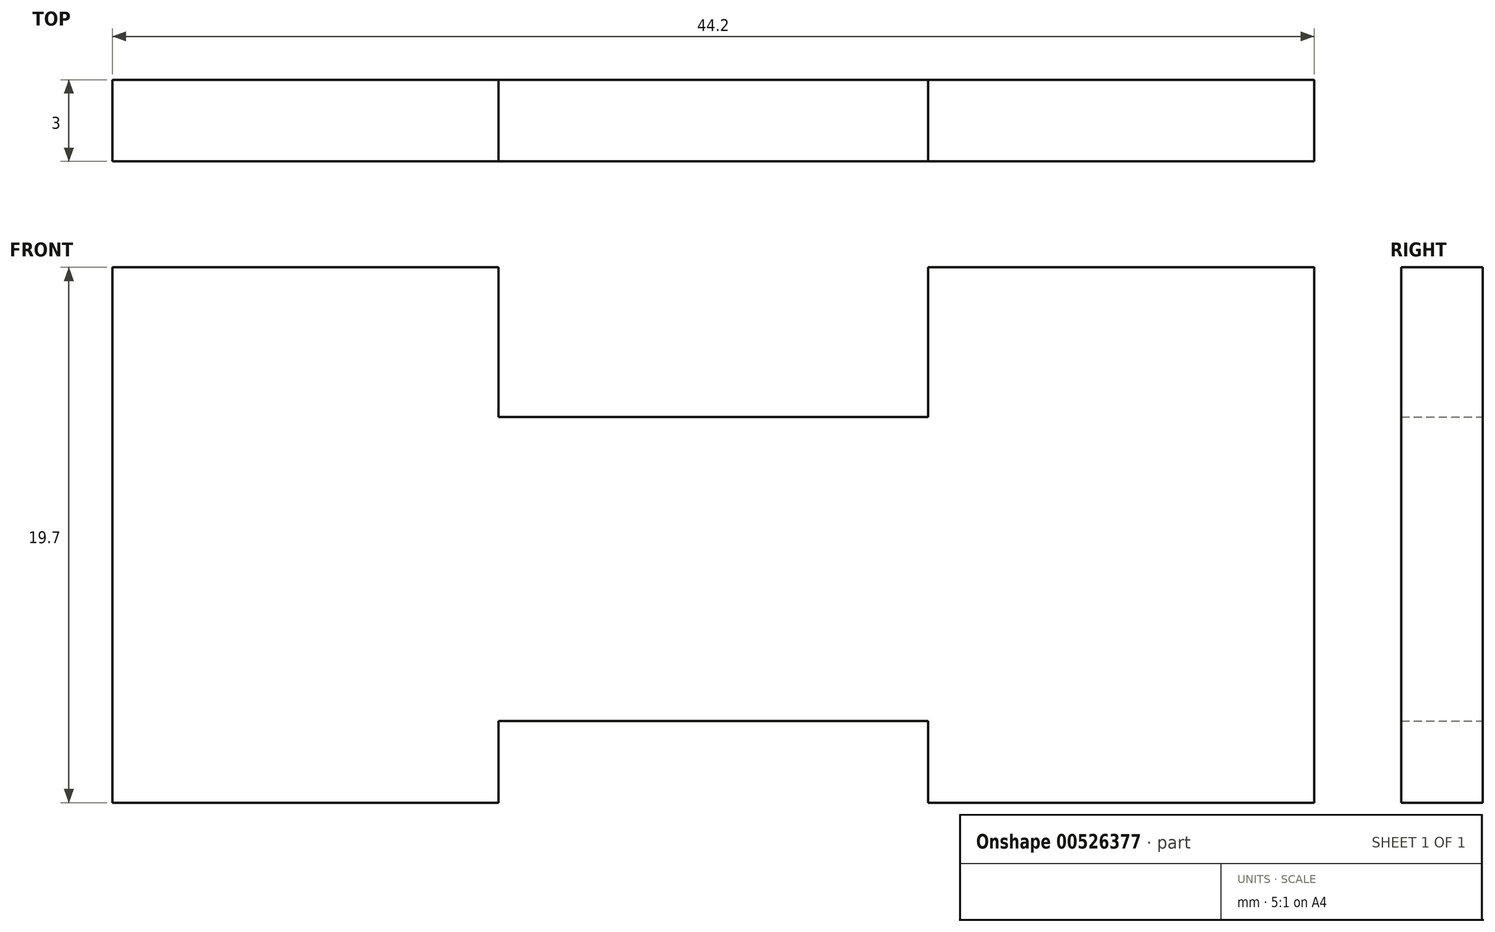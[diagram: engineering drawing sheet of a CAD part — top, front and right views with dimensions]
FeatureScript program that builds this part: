
annotation { "Feature Type Name" : "Feature", "Feature Type Description" : "" }
export const myFeature = defineFeature(function(context is Context, id is Id, definition is map)
    precondition{}
    {
        {
            assignVariable(context, id + "F0", {"name" : "thickness", "anyValue" : 3});
        }
        {
            var Q0;
            Q0=qCreatedBy(makeId("Front.planeOp"),FACE);
            var sketch = newSketch(context, id + "F1", { "sketchPlane" : qUnion([Q0])});
            skLineSegment(sketch, "E0.top", {"start": v(22.5, 10.25) * mm, "end": v(-22.5, 10.25) * mm, "construction": true});
            skLineSegment(sketch, "E0.left", {"start": v(22.5, -10.25) * mm, "end": v(22.5, 10.25) * mm, "construction": true});
            skLineSegment(sketch, "E0.right", {"start": v(-22.5, -10.25) * mm, "end": v(-22.5, 10.25) * mm, "construction": true});
            skPoint(sketch, "E0.middle", {"position": v(0, 0) * mm});
            skLineSegment(sketch, "E1", {"start": v(-22.5, -10.25) * mm, "end": v(-7.5, -10.25) * mm, "construction": true});
            skLineSegment(sketch, "E2", {"start": v(-7.5, -10.25) * mm, "end": v(-7.5, -7.25) * mm, "construction": true});
            skLineSegment(sketch, "E3", {"start": v(-7.5, -7.25) * mm, "end": v(7.5, -7.25) * mm, "construction": true});
            skLineSegment(sketch, "E4", {"start": v(7.5, -7.25) * mm, "end": v(7.5, -10.25) * mm, "construction": true});
            skLineSegment(sketch, "E5", {"start": v(7.5, -10.25) * mm, "end": v(22.5, -10.25) * mm, "construction": true});
            skLineSegment(sketch, "E6", {"start": v(-22.5, 10.25) * mm, "end": v(-7.5, 10.25) * mm, "construction": true});
            skLineSegment(sketch, "E7", {"start": v(-7.5, 10.25) * mm, "end": v(-7.5, 4.75) * mm, "construction": true});
            skLineSegment(sketch, "E8", {"start": v(-7.5, 4.75) * mm, "end": v(7.5, 4.75) * mm, "construction": true});
            skLineSegment(sketch, "E9", {"start": v(7.5, 4.75) * mm, "end": v(7.5, 10.25) * mm, "construction": true});
            skLineSegment(sketch, "E10", {"start": v(7.5, 10.25) * mm, "end": v(22.5, 10.25) * mm, "construction": true});
            skLineSegment(sketch, "E11.0", {"start": v(-22.1, -9.85) * mm, "end": v(-22.1, 9.85) * mm});
            skLineSegment(sketch, "E11.1", {"start": v(7.9, -9.85) * mm, "end": v(22.1, -9.85) * mm});
            skLineSegment(sketch, "E11.2", {"start": v(7.9, -6.85) * mm, "end": v(7.9, -9.85) * mm});
            skLineSegment(sketch, "E11.3", {"start": v(-7.9, -6.85) * mm, "end": v(7.9, -6.85) * mm});
            skLineSegment(sketch, "E11.4", {"start": v(-7.9, -9.85) * mm, "end": v(-7.9, -6.85) * mm});
            skLineSegment(sketch, "E11.5", {"start": v(22.1, -9.85) * mm, "end": v(22.1, 9.85) * mm});
            skLineSegment(sketch, "E11.6", {"start": v(-22.1, -9.85) * mm, "end": v(-7.9, -9.85) * mm});
            skLineSegment(sketch, "E11.7", {"start": v(7.9, 9.85) * mm, "end": v(22.1, 9.85) * mm});
            skLineSegment(sketch, "E11.8", {"start": v(7.9, 4.35) * mm, "end": v(7.9, 9.85) * mm});
            skLineSegment(sketch, "E11.9", {"start": v(-7.9, 4.35) * mm, "end": v(7.9, 4.35) * mm});
            skLineSegment(sketch, "E11.10", {"start": v(-7.9, 9.85) * mm, "end": v(-7.9, 4.35) * mm});
            skLineSegment(sketch, "E11.11", {"start": v(-22.1, 9.85) * mm, "end": v(-7.9, 9.85) * mm});
            skSolve(sketch);
        }
        {
            var Q0;
            Q0 = qSketchRegion(id + "F1", true);
            extrude(context, id + "F2", {"entities" : qUnion([Q0]), "depth" : (getVariable(context, 'thickness')) * mm, "offsetDistance" : 25 * mm});
        }
    });
